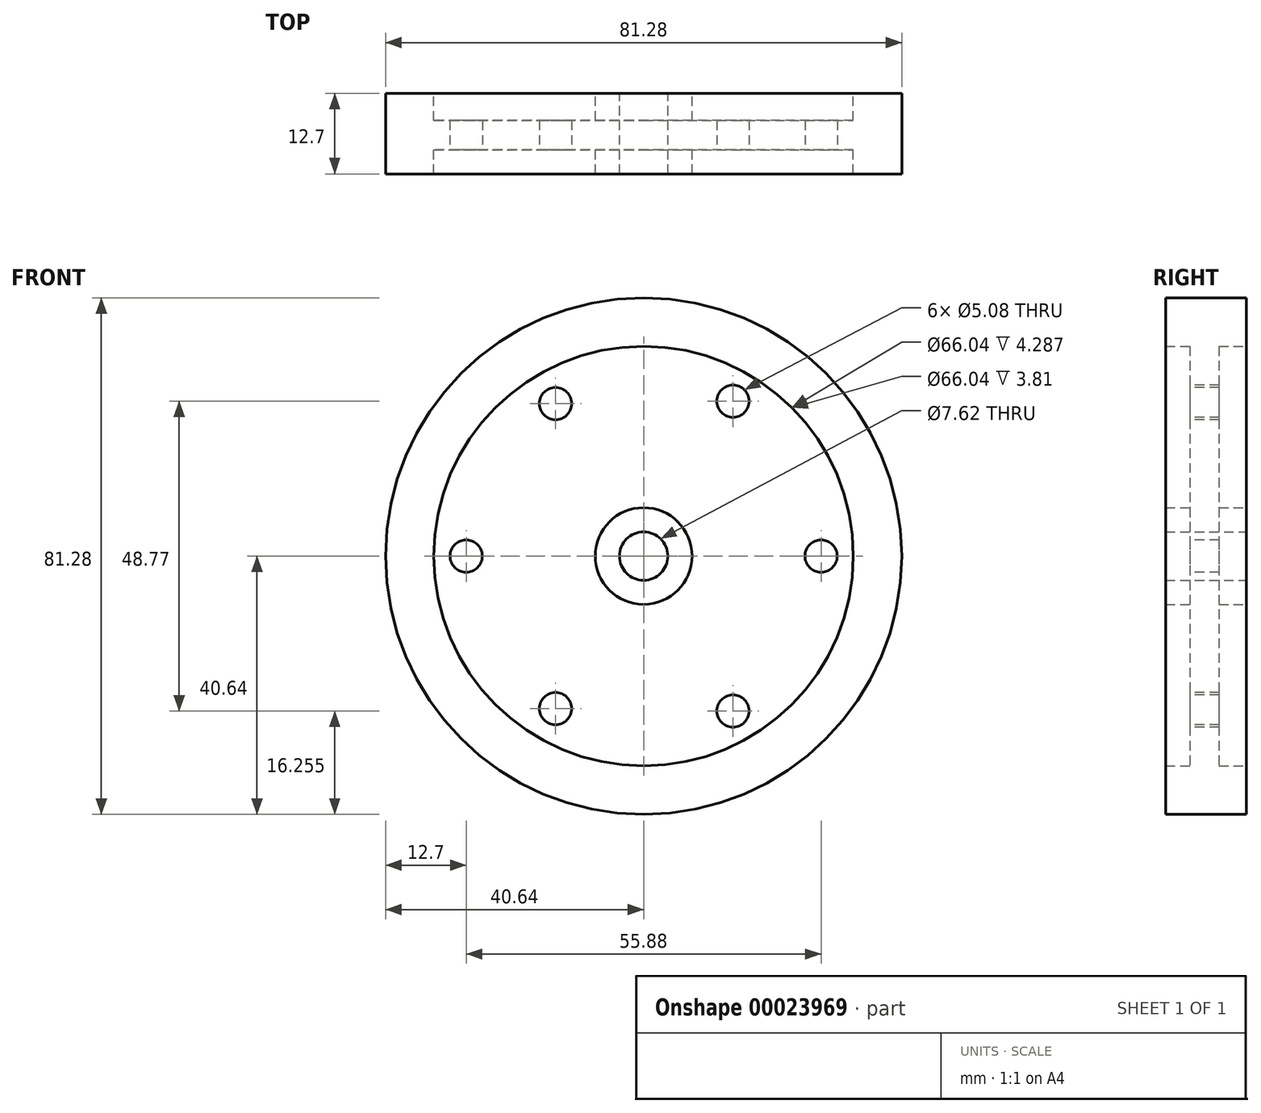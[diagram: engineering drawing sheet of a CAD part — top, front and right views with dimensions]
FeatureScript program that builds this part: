
annotation { "Feature Type Name" : "Feature", "Feature Type Description" : "" }
export const myFeature = defineFeature(function(context is Context, id is Id, definition is map)
    precondition{}
    {
        {
            var Q0;
            Q0=qCreatedBy(makeId("Top.planeOp"),FACE);
            var sketch = newSketch(context, id + "F0", { "sketchPlane" : qUnion([Q0])});
            skLineSegment(sketch, "E0", {"start": v(0, 32.62) * mm, "end": v(0, -32.47) * mm, "construction": true});
            skLineSegment(sketch, "E1.bottom", {"start": v(-33.02, 0) * mm, "end": v(-40.64, 0) * mm});
            skLineSegment(sketch, "E1.top", {"start": v(-33.02, 12.7) * mm, "end": v(-40.64, 12.7) * mm});
            skLineSegment(sketch, "E1.left", {"start": v(0, 0) * mm, "end": v(0, 12.7) * mm});
            skLineSegment(sketch, "E1.right", {"start": v(-40.64, 0) * mm, "end": v(-40.64, 12.7) * mm});
            skLineSegment(sketch, "E2.top", {"start": v(0, 3.81) * mm, "end": v(-3.81, 3.81) * mm});
            skLineSegment(sketch, "E2.left", {"start": v(0, 0) * mm, "end": v(0, 3.81) * mm});
            skLineSegment(sketch, "E2.right", {"start": v(-33.02, 0) * mm, "end": v(-33.02, 3.8) * mm});
            skLineSegment(sketch, "E3.top", {"start": v(0, 8.41) * mm, "end": v(-3.81, 8.41) * mm});
            skLineSegment(sketch, "E3.left", {"start": v(0, 12.7) * mm, "end": v(0, 8.41) * mm});
            skLineSegment(sketch, "E3.right", {"start": v(-33.02, 12.7) * mm, "end": v(-33.02, 8.41) * mm});
            skLineSegment(sketch, "E4.bottom", {"start": v(-7.62, 12.7) * mm, "end": v(-3.81, 12.7) * mm});
            skLineSegment(sketch, "E4.top", {"start": v(-7.62, 0) * mm, "end": v(-3.81, 0) * mm});
            skLineSegment(sketch, "E4.left", {"start": v(-7.62, 12.7) * mm, "end": v(-7.62, 8.41) * mm});
            skLineSegment(sketch, "E4.right", {"start": v(-3.81, 12.7) * mm, "end": v(-3.81, 8.41) * mm});
            skLineSegment(sketch, "E5.trimOffspring", {"start": v(-7.62, 8.41) * mm, "end": v(-33.02, 8.41) * mm});
            skLineSegment(sketch, "E6.trimOffspring", {"start": v(-7.62, 3.81) * mm, "end": v(-33.02, 3.8) * mm});
            skLineSegment(sketch, "E7.trimOffspring", {"start": v(-3.81, 3.81) * mm, "end": v(-3.81, 0) * mm});
            skLineSegment(sketch, "E8.trimOffspring", {"start": v(-7.62, 3.81) * mm, "end": v(-7.62, 0) * mm});
            skSolve(sketch);
        }
        {
            var Q0;
            Q0=makeQuery(id+"F0.imprint","IMPRINT",FACE,{"disambiguationData":[TD([[makeQuery(id+"F0.imprint","IMPRINT",EDGE,{"derivedFrom":sQuery(id+"F0.wireOp",EDGE,"E1.bottom")}),-1.0]])]});
            var Q1;
            Q1=sQuery(id+"F0.wireOp",EDGE,"E0");
            revolve(context, id + "F1", {"entities" : qUnion([Q0]), "axis" : qUnion([Q1]), "revolveType" : RevolveType.FULL});
        }
        {
            var Q0;
            Q0=qCreatedBy(makeId("Front.planeOp"),FACE);
            var sketch = newSketch(context, id + "F2", { "sketchPlane" : qUnion([Q0])});
            skLineSegment(sketch, "E9", {"start": v(0, 0) * mm, "end": v(-76.3, 0) * mm, "construction": true});
            skLineSegment(sketch, "E10", {"start": v(-76.3, 0) * mm, "end": v(83.6, 0) * mm, "construction": true});
            skLineSegment(sketch, "E11", {"start": v(0, 0) * mm, "end": v(0, 64.47) * mm, "construction": true});
            skLineSegment(sketch, "E12", {"start": v(0, 64.47) * mm, "end": v(0, -89.85) * mm, "construction": true});
            skCircle(sketch, "E13", {"center": v(-27.94, 0) * mm, "radius": 2.54 * mm});
            skCircle(sketch, "E14", {"center": v(27.94, 0) * mm, "radius": 2.54 * mm});
            skLineSegment(sketch, "E15", {"start": v(33.02, 0) * mm, "end": v(-16.51, 28.6) * mm, "construction": true});
            skLineSegment(sketch, "E16", {"start": v(-16.51, 28.6) * mm, "end": v(-16.51, -28.6) * mm, "construction": true});
            skLineSegment(sketch, "E17", {"start": v(-16.51, -28.6) * mm, "end": v(33.02, 0) * mm, "construction": true});
            skLineSegment(sketch, "E18", {"start": v(-16.51, -28.6) * mm, "end": v(0, 0) * mm, "construction": true});
            skLineSegment(sketch, "E19", {"start": v(-16.51, 28.6) * mm, "end": v(0, 0) * mm, "construction": true});
            skLineSegment(sketch, "E20", {"start": v(0, 0) * mm, "end": v(21.82, -37.8) * mm, "construction": true});
            skLineSegment(sketch, "E21", {"start": v(0, 0) * mm, "end": v(21.82, 37.8) * mm, "construction": true});
            skCircle(sketch, "E22", {"center": v(14.08, 24.38) * mm, "radius": 2.54 * mm});
            skCircle(sketch, "E23", {"center": v(-13.86, -24) * mm, "radius": 2.54 * mm});
            skCircle(sketch, "E24", {"center": v(-13.86, 24) * mm, "radius": 2.54 * mm});
            skCircle(sketch, "E25", {"center": v(14.08, -24.38) * mm, "radius": 2.54 * mm});
            skSolve(sketch);
        }
        {
            var Q0;
            Q0=makeQuery(id+"F2.imprint","IMPRINT",FACE,{"disambiguationData":[TD([[makeQuery(id+"F2.imprint","IMPRINT",EDGE,{"derivedFrom":sQuery(id+"F2.wireOp",EDGE,"E24")}),1.0]])]});
            var Q1;
            Q1=makeQuery(id+"F2.imprint","IMPRINT",FACE,{"disambiguationData":[TD([[makeQuery(id+"F2.imprint","IMPRINT",EDGE,{"derivedFrom":sQuery(id+"F2.wireOp",EDGE,"E22")}),1.0]])]});
            var Q2;
            Q2=makeQuery(id+"F2.imprint","IMPRINT",FACE,{"disambiguationData":[TD([[makeQuery(id+"F2.imprint","IMPRINT",EDGE,{"derivedFrom":sQuery(id+"F2.wireOp",EDGE,"E14")}),1.0]])]});
            var Q3;
            Q3=makeQuery(id+"F2.imprint","IMPRINT",FACE,{"disambiguationData":[TD([[makeQuery(id+"F2.imprint","IMPRINT",EDGE,{"derivedFrom":sQuery(id+"F2.wireOp",EDGE,"E25")}),1.0]])]});
            var Q4;
            Q4=makeQuery(id+"F2.imprint","IMPRINT",FACE,{"disambiguationData":[TD([[makeQuery(id+"F2.imprint","IMPRINT",EDGE,{"derivedFrom":sQuery(id+"F2.wireOp",EDGE,"E23")}),1.0]])]});
            var Q5;
            Q5=makeQuery(id+"F2.imprint","IMPRINT",FACE,{"disambiguationData":[TD([[makeQuery(id+"F2.imprint","IMPRINT",EDGE,{"derivedFrom":sQuery(id+"F2.wireOp",EDGE,"E13")}),1.0]])]});
            extrude(context, id + "F3", {"entities" : qUnion([Q0, Q1, Q2, Q3, Q4, Q5]), "operationType" : NewBodyOperationType.REMOVE, "oppositeDirection" : true, "depth" : 25.4 * mm});
        }
        {
            var Q0;
            Q0=makeQuery(id+"F1.opRevolve","SWEPT_FACE",FACE,{"disambiguationData":[OSD([sQuery(id+"F0.wireOp",EDGE,"E2.top")])]});
            extrude(context, id + "F4", {"entities" : qUnion([Q0]), "operationType" : NewBodyOperationType.REMOVE, "oppositeDirection" : true, "depth" : 25.4 * mm});
        }
    });
